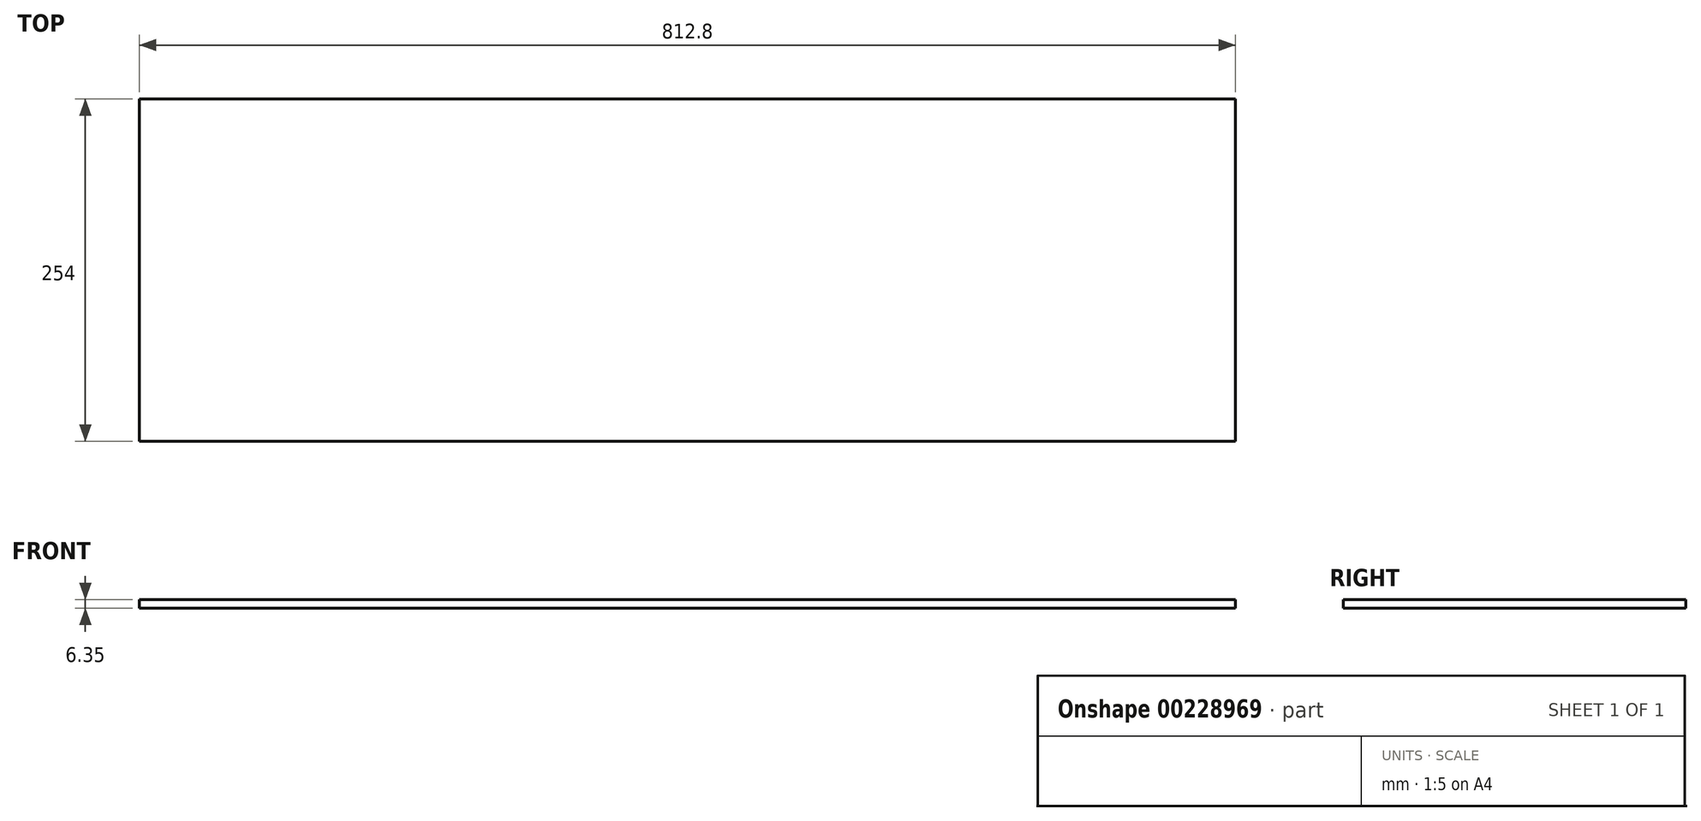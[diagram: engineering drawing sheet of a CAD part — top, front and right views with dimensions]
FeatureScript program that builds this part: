
annotation { "Feature Type Name" : "Feature", "Feature Type Description" : "" }
export const myFeature = defineFeature(function(context is Context, id is Id, definition is map)
    precondition{}
    {
        {
            var Q0;
            Q0=qCreatedBy(makeId("Top.planeOp"),FACE);
            var sketch = newSketch(context, id + "F0", { "sketchPlane" : qUnion([Q0])});
            skLineSegment(sketch, "E0.bottom", {"start": v(0, 0) * mm, "end": v(812.8, 0) * mm});
            skLineSegment(sketch, "E0.top", {"start": v(0, 254) * mm, "end": v(812.8, 254) * mm});
            skLineSegment(sketch, "E0.left", {"start": v(0, 0) * mm, "end": v(0, 254) * mm});
            skLineSegment(sketch, "E0.right", {"start": v(812.8, 0) * mm, "end": v(812.8, 254) * mm});
            skSolve(sketch);
        }
        {
            var Q0;
            Q0 = qSketchRegion(id + "F0", true);
            extrude(context, id + "F1", {"entities" : qUnion([Q0]), "depth" : 6.35 * mm});
        }
    });
